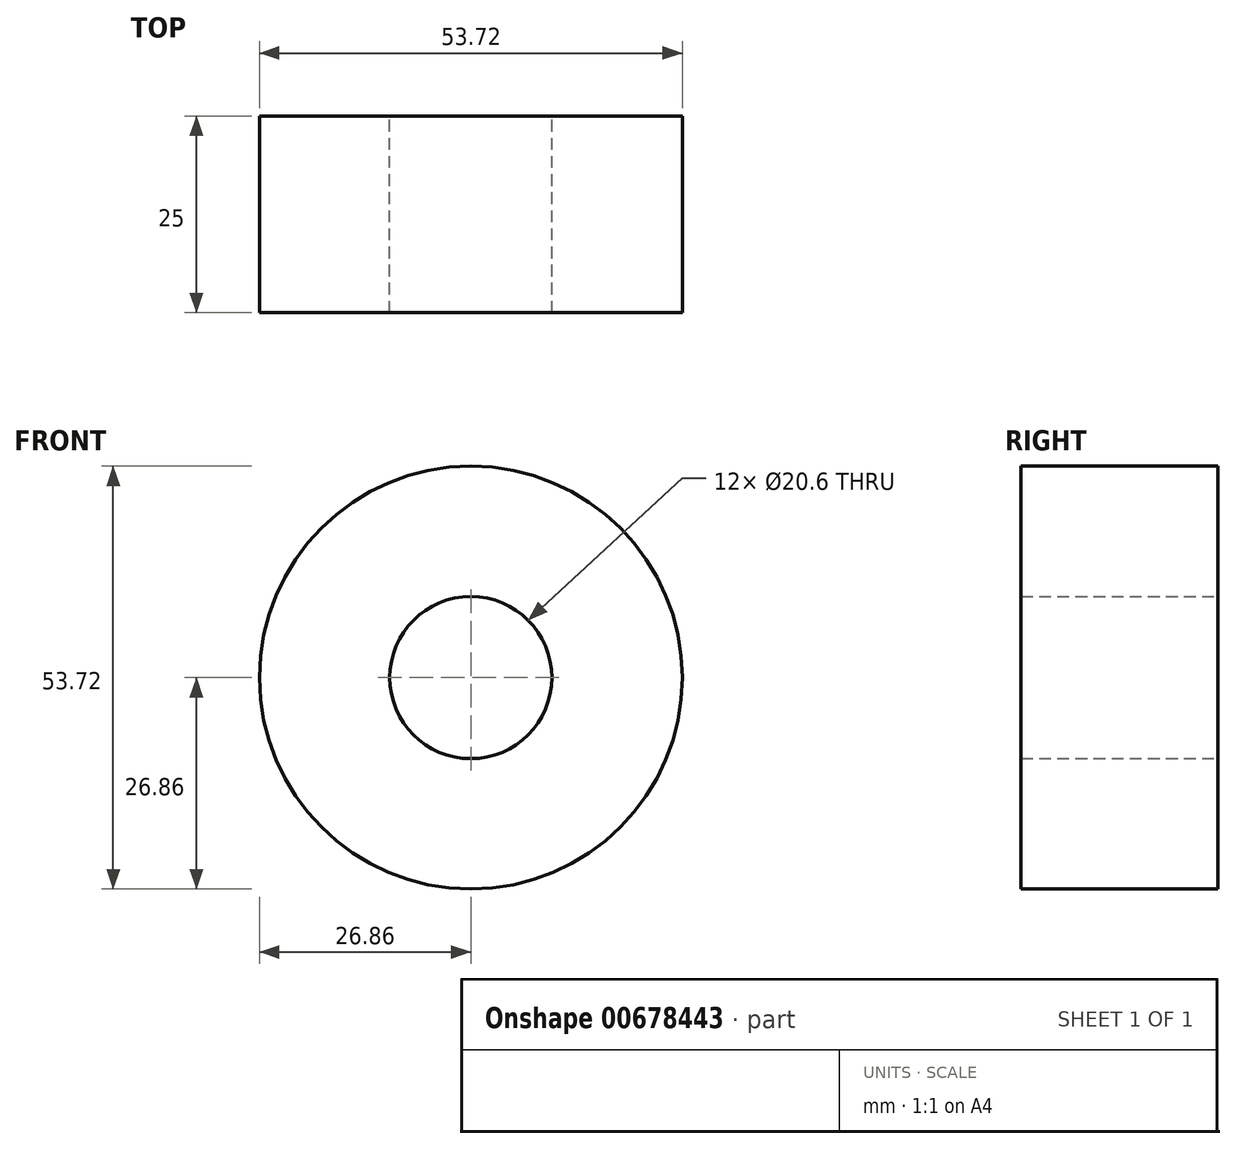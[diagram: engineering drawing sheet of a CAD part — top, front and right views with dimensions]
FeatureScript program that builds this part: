
annotation { "Feature Type Name" : "Feature", "Feature Type Description" : "" }
export const myFeature = defineFeature(function(context is Context, id is Id, definition is map)
    precondition{}
    {
        {
            var Q0;
            Q0=qCreatedBy(makeId("Front.planeOp"),FACE);
            var sketch = newSketch(context, id + "F0", { "sketchPlane" : qUnion([Q0])});
            skCircle(sketch, "E0", {"center": v(0, 0) * mm, "radius": 31.75 * mm, "construction": true});
            skCircle(sketch, "E1", {"center": v(0, 0) * mm, "radius": 29.34 * mm, "construction": true});
            skCircle(sketch, "E2", {"center": v(0, 0) * mm, "radius": 26.86 * mm});
            skLineSegment(sketch, "E3", {"start": v(0, 0) * mm, "end": v(0, 63.37) * mm, "construction": true});
            skLineSegment(sketch, "E4", {"start": v(0, 0) * mm, "end": v(-4.15, 63.37) * mm, "construction": true});
            skLineSegment(sketch, "E5", {"start": v(0, 29.34) * mm, "end": v(-60.02, 29.34) * mm, "construction": true});
            skLineSegment(sketch, "E6", {"start": v(0, 29.34) * mm, "end": v(-56.34, 8.83) * mm, "construction": true});
            skCircle(sketch, "E7", {"center": v(0, 0) * mm, "radius": 27.57 * mm, "construction": true});
            skCircle(sketch, "E8", {"center": v(0, 29.34) * mm, "radius": 14.6 * mm, "construction": true});
            skCircle(sketch, "E9", {"center": v(-13.72, 24.34) * mm, "radius": 14.6 * mm, "construction": true});
            skArc(sketch, "E10.MirrorCS", {"start": v(-5.95, 31.17) * mm, "mid": v(-5.08, 33.82) * mm, "end": v(-3.74, 36.27) * mm});
            skArc(sketch, "E11.MirrorCS", {"start": v(-6.18, 26.14) * mm, "mid": v(-6.28, 28.67) * mm, "end": v(-5.95, 31.17) * mm});
            skArc(sketch, "E12.MirrorCS", {"start": v(1.83, 31.68) * mm, "mid": v(0.62, 34.2) * mm, "end": v(-1.03, 36.45) * mm});
            skArc(sketch, "E13.MirrorCS", {"start": v(2.71, 26.72) * mm, "mid": v(2.48, 29.24) * mm, "end": v(1.83, 31.68) * mm});
            skArc(sketch, "E14", {"start": v(-1.03, 36.45) * mm, "mid": v(-2.41, 36.79) * mm, "end": v(-3.74, 36.27) * mm});
            skCircle(sketch, "E15", {"center": v(0, 0) * mm, "radius": 10.3 * mm});
            skSolve(sketch);
        }
        {
            var Q0;
            {var subQ0=sQuery(id+"F0.wireOp",EDGE,"E2");var subQ1=makeQuery(id+"F0.imprint","INTERSECT",VERTEX,{"derivedFrom":[subQ0,sQuery(id+"F0.wireOp",EDGE,"E11.MirrorCS")]});Q0=makeQuery(id+"F0.imprint","IMPRINT",FACE,{"disambiguationData":[TD([[makeQuery(id+"F0.imprint","IMPRINT",EDGE,{"disambiguationData":[TD([[subQ1,1.0]])],"derivedFrom":subQ0}),1.0]])]});}
            var Q1;
            Q1=makeQuery(id+"F0.imprint","IMPRINT",FACE,{"disambiguationData":[TD([[makeQuery(id+"F0.imprint","IMPRINT",EDGE,{"derivedFrom":sQuery(id+"F0.wireOp",EDGE,"E10.MirrorCS")}),-1.0]])]});
            extrude(context, id + "F1", {"entities" : qUnion([Q0, Q1]), "depth" : 25 * mm, "offsetDistance" : 25 * mm});
        }
        {
            var Q0;
            Q0=makeQuery(id+"F1.opExtrude","SWEPT_BODY",BODY,{"disambiguationData":[OSD([sQuery(id+"F0.wireOp",EDGE,"E2"),sQuery(id+"F0.wireOp",EDGE,"E10.MirrorCS"),sQuery(id+"F0.wireOp",EDGE,"E11.MirrorCS"),sQuery(id+"F0.wireOp",EDGE,"E12.MirrorCS"),sQuery(id+"F0.wireOp",EDGE,"E13.MirrorCS"),sQuery(id+"F0.wireOp",EDGE,"E14")])]});
            var Q1;
            Q1=makeQuery(id+"F1.opExtrude","SWEPT_FACE",FACE,{"disambiguationData":[OSD([sQuery(id+"F0.wireOp",EDGE,"E2")])]});
            circularPattern(context, id + "F2", {"entities" : qUnion([Q0]), "axis" : qUnion([Q1]), "angle" : 360 * degree, "instanceCount" : 12, "equalSpace" : true});
        }
    });
